# Revit family: KEUCO_56080010100
name_source: partatom
category: Sanitärinstallationen
revit_build: Autodesk Revit 2016 (Build: 20150220_1215(x64)
units: mm (PartAtom-declared; Revit-internal decimal feet)

## family parameters
Arbeitsebenenbasiert = Nein
Beim Laden mit Abzugskörper schneiden = Nein
Bemaßung runder Anschluss = Durchmesser verwenden
Gemeinsam genutzt = Nein
Immer vertikal = Ja
OmniClass-Nummer = 23.45.00.00
Raumberechnungspunkt = Nein
Teiletyp = Normal

## types (1)
- 56080010100
    Artikelnummer = 56080010100
    Ausschreibungstext = KEUCO  Stabhandbrause 56080010100
Hochglanzverchromte Handbrause
Mit Normalstrahl
Geräuschverhalten DIN 4109 Gruppe I,
    Beschreibung = mit Normalstrahl, geräuschgeprüft
    Gewicht = 1.042
    Hersteller = KEUCO
    Kategorie = ARM
    KreisBase = Ja
    Preisgruppe = 1
    Serie = IXMO
    URL = https://www.keuco.com
    Verwendung = DU / WA
    ViereckBase = Nein

## geometry (parser evidence)
native form markers: Blend x2, Sweep x3
no freeform markers — native parametric forms only
